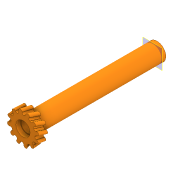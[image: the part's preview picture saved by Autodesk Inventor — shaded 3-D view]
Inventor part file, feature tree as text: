
AUTODESK INVENTOR PART (.ipt)
format: ipt  version: 2020 (Build 240168000, 168)  size: 343,552 bytes
history: native  units: in
note: dims shown in document units (in); Inventor stores cm internally (conversion verified against a paired STEP export)
features: sketch x5, extrude x3, plane x2, sweep x1, other x1
ambient origin geometry x8: Origin, YZ Plane, XZ Plane, XY Plane, X Axis, Y Axis, Z Axis, Center Point
bodies: Solid1 (feature_tree)
feature tree (12):
  extrude  "Extrusion1"  Depth=0.3937in
  plane  "Work Plane1"
  sweep  "Sweep1"
  extrude  "Extrusion3"  Depth=0.0866in
  plane  "Work Plane2"
  extrude  "Extrusion4"  Depth=2.7953in
  sketch  "Sketch1"  dims[d0=0.3937in d1=0.315in]
  sketch  "Sketch3"  dims[d2=2.9921in d3=0.0in d7=-0.1969in]
  sketch  "3D Sketch1"
  other  "Helical Curve1"
  sketch  "Sketch4"  dims[d8=0.7087in d9=0.0866in]
  sketch  "Sketch5"  dims[d10=0.0787in d11=0.0787in d12=0.0787in d13=4.7244in d15=360.0deg d17=0.1969in d18=0.0118in d19=0.535in d20=0.0in d21=0.0in d22=0.0in d23=0.1969in d24=0.1969in d25=0.0787in d26=2.9921in d27=0.0in d28=-0.0984in d29=0.2756in d30=2.7953in d31=0.0in]
